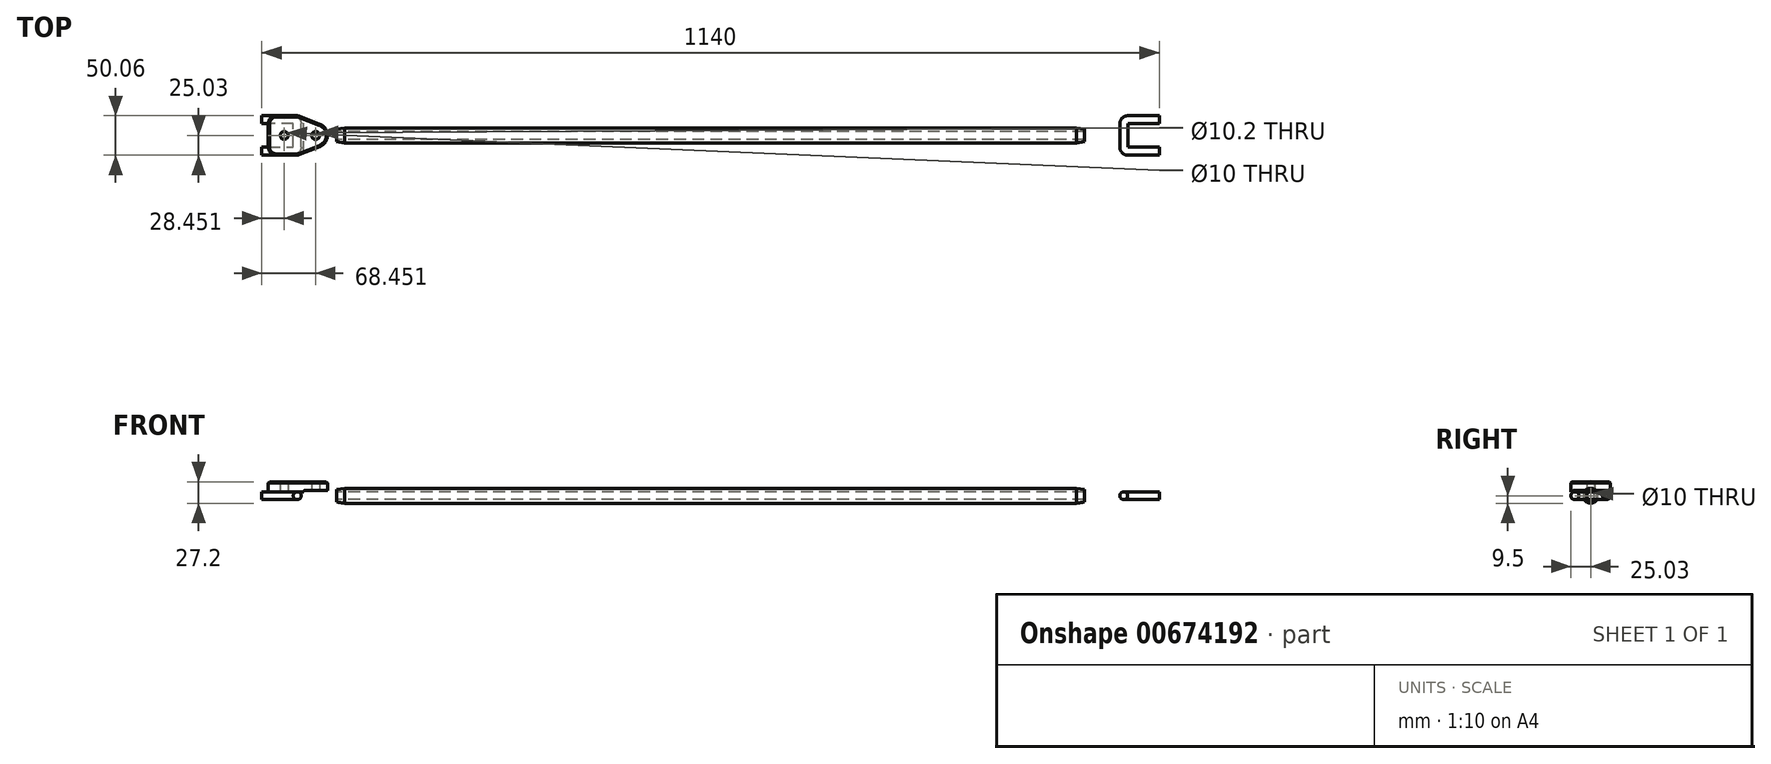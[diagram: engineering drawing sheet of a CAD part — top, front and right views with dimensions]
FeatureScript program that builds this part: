
annotation { "Feature Type Name" : "Feature", "Feature Type Description" : "" }
export const myFeature = defineFeature(function(context is Context, id is Id, definition is map)
    precondition{}
    {
        {
            var Q0;
            Q0=qCreatedBy(makeId("Top.planeOp"),FACE);
            var sketch = newSketch(context, id + "F0", { "sketchPlane" : qUnion([Q0])});
            skLineSegment(sketch, "E0", {"start": v(-525, 0) * mm, "end": v(525, 0) * mm, "construction": true});
            skLineSegment(sketch, "E1", {"start": v(525, 15) * mm, "end": v(525, -15) * mm});
            skLineSegment(sketch, "E2", {"start": v(530, -20) * mm, "end": v(570, -20) * mm});
            skLineSegment(sketch, "E3", {"start": v(530, 20) * mm, "end": v(570, 20) * mm});
            skPoint(sketch, "E4.visualSharp", {"position": v(525, 20) * mm});
            skArc(sketch, "E4.filletArc", {"start": v(530, 20) * mm, "mid": v(526.46, 18.54) * mm, "end": v(525, 15) * mm});
            skPoint(sketch, "E5.visualSharp", {"position": v(525, -20) * mm});
            skArc(sketch, "E5.filletArc", {"start": v(525, -15) * mm, "mid": v(526.46, -18.54) * mm, "end": v(530, -20) * mm});
            skArc(sketch, "E6.MirrorCS", {"start": v(-525, -15) * mm, "mid": v(-526.46, -18.54) * mm, "end": v(-530, -20) * mm});
            skArc(sketch, "E7.MirrorCS", {"start": v(-530, 20) * mm, "mid": v(-526.46, 18.54) * mm, "end": v(-525, 15) * mm});
            skPoint(sketch, "E8.MirrorP", {"position": v(-525, 20) * mm});
            skPoint(sketch, "E9.MirrorP", {"position": v(-525, -20) * mm});
            skLineSegment(sketch, "E10.MirrorCS", {"start": v(-530, -20) * mm, "end": v(-570, -20) * mm});
            skLineSegment(sketch, "E11.MirrorCS", {"start": v(-525, 15) * mm, "end": v(-525, -15) * mm});
            skLineSegment(sketch, "E12.MirrorCS", {"start": v(-530, 20) * mm, "end": v(-570, 20) * mm});
            skSolve(sketch);
        }
        {
            var Q0;
            Q0=qCreatedBy(makeId("Right.planeOp"),FACE);
            cPlane(context, id + "F1", {"entities" : qUnion([Q0]), "cplaneType" : CPlaneType.OFFSET, "offset" : 570 * mm, "width" : 150 * mm, "height" : 150 * mm});
        }
        {
            var Q0;
            Q0=qCreatedBy(makeId("Right.planeOp"),FACE);
            cPlane(context, id + "F2", {"entities" : qUnion([Q0]), "cplaneType" : CPlaneType.OFFSET, "offset" : 570 * mm, "oppositeDirection" : true, "width" : 150 * mm, "height" : 150 * mm});
        }
        {
            var Q0;
            Q0=qCreatedBy(id+"F2.planeOp",FACE);
            var sketch = newSketch(context, id + "F3", { "sketchPlane" : qUnion([Q0])});
            skCircle(sketch, "E13", {"center": v(-20.03, 0) * mm, "radius": 5 * mm});
            skLineSegment(sketch, "E14", {"start": v(0, 9.48) * mm, "end": v(0, -9.24) * mm, "construction": true});
            skSolve(sketch);
        }
        {
            var Q0;
            Q0=makeQuery(id+"F3.imprint","IMPRINT",FACE,{"disambiguationData":[TD([[makeQuery(id+"F3.imprint","IMPRINT",EDGE,{"derivedFrom":sQuery(id+"F3.wireOp",EDGE,"E13")}),1.0]])]});
            var Q1;
            Q1=sQuery(id+"F0.wireOp",EDGE,"E10.MirrorCS");
            var Q2;
            Q2=sQuery(id+"F0.wireOp",EDGE,"E6.MirrorCS");
            var Q3;
            Q3=sQuery(id+"F0.wireOp",EDGE,"E11.MirrorCS");
            var Q4;
            Q4=sQuery(id+"F0.wireOp",EDGE,"E7.MirrorCS");
            var Q5;
            Q5=sQuery(id+"F0.wireOp",EDGE,"E12.MirrorCS");
            sweep(context, id + "F4", {"profiles" : qUnion([Q0]), "path" : qUnion([Q1, Q2, Q3, Q4, Q5])});
        }
        {
            var Q0;
            Q0=qCreatedBy(id+"F1.planeOp",FACE);
            var sketch = newSketch(context, id + "F5", { "sketchPlane" : qUnion([Q0])});
            skCircle(sketch, "E15", {"center": v(20, 0) * mm, "radius": 5 * mm});
            skLineSegment(sketch, "E16", {"start": v(0, 9.53) * mm, "end": v(0, -12.38) * mm, "construction": true});
            skSolve(sketch);
        }
        {
            var Q0;
            Q0=makeQuery(id+"F5.imprint","IMPRINT",FACE,{"disambiguationData":[TD([[makeQuery(id+"F5.imprint","IMPRINT",EDGE,{"derivedFrom":sQuery(id+"F5.wireOp",EDGE,"E15")}),1.0]])]});
            var Q1;
            Q1=sQuery(id+"F0.wireOp",EDGE,"E3");
            var Q2;
            Q2=sQuery(id+"F0.wireOp",EDGE,"E4.filletArc");
            var Q3;
            Q3=sQuery(id+"F0.wireOp",EDGE,"E1");
            var Q4;
            Q4=sQuery(id+"F0.wireOp",EDGE,"E5.filletArc");
            var Q5;
            Q5=sQuery(id+"F0.wireOp",EDGE,"E2");
            sweep(context, id + "F6", {"profiles" : qUnion([Q0]), "path" : qUnion([Q1, Q2, Q3, Q4, Q5])});
        }
        {
            var Q0;
            Q0=qCreatedBy(makeId("Right.planeOp"),FACE);
            var sketch = newSketch(context, id + "F7", { "sketchPlane" : qUnion([Q0])});
            skCircle(sketch, "E17", {"center": v(0, 0) * mm, "radius": 9.5 * mm});
            skCircle(sketch, "E18", {"center": v(0, 0) * mm, "radius": 5 * mm});
            skSolve(sketch);
        }
        {
            var Q0;
            Q0=makeQuery(id+"F7.imprint","IMPRINT",FACE,{"disambiguationData":[TD([[makeQuery(id+"F7.imprint","IMPRINT",EDGE,{"derivedFrom":sQuery(id+"F7.wireOp",EDGE,"E17")}),1.0]])]});
            extrude(context, id + "F8", {"entities" : qUnion([Q0]), "endBound" : BoundingType.SYMMETRIC, "depth" : 950 * mm, "offsetDistance" : 25 * mm});
        }
        {
            var Q0;
            Q0=qCreatedBy(makeId("Top.planeOp"),FACE);
            cPlane(context, id + "F9", {"entities" : qUnion([Q0]), "cplaneType" : CPlaneType.OFFSET, "offset" : 5 * mm, "width" : 150 * mm, "height" : 150 * mm});
        }
        {
            var Q0;
            Q0=qCreatedBy(id+"F9.planeOp",FACE);
            var sketch = newSketch(context, id + "F10", { "sketchPlane" : qUnion([Q0])});
            skLineSegment(sketch, "E19.bottom", {"start": v(-525.95, 25) * mm, "end": v(-551.55, 25) * mm});
            skLineSegment(sketch, "E19.top", {"start": v(-525.95, -25) * mm, "end": v(-551.55, -25) * mm});
            skLineSegment(sketch, "E19.right", {"start": v(-561.55, 15) * mm, "end": v(-561.55, -15) * mm});
            skPoint(sketch, "E19.middle", {"position": v(-524.05, 0) * mm});
            skLineSegment(sketch, "E20", {"start": v(-524.05, 0) * mm, "end": v(-486.55, 0) * mm, "construction": true});
            skArc(sketch, "E21", {"start": v(-496.04, -13.95) * mm, "mid": v(-486.55, 0) * mm, "end": v(-496.04, 13.95) * mm});
            skLineSegment(sketch, "E22", {"start": v(-496.04, 13.95) * mm, "end": v(-522.28, 24.3) * mm});
            skLineSegment(sketch, "E23", {"start": v(-496.04, -13.95) * mm, "end": v(-522.28, -24.3) * mm});
            skCircle(sketch, "E24", {"center": v(-501.55, 0) * mm, "radius": 5.1 * mm});
            skPoint(sketch, "E25.orphan", {"position": v(-486.55, -25) * mm});
            skPoint(sketch, "E19.left.start.orphan", {"position": v(-486.55, 25) * mm});
            skPoint(sketch, "E26.visualSharp", {"position": v(-524.05, 25) * mm});
            skArc(sketch, "E26.filletArc", {"start": v(-522.28, 24.3) * mm, "mid": v(-524.08, 24.82) * mm, "end": v(-525.95, 25) * mm});
            skPoint(sketch, "E27.visualSharp", {"position": v(-561.55, 25) * mm});
            skArc(sketch, "E27.filletArc", {"start": v(-551.55, 25) * mm, "mid": v(-558.62, 22.07) * mm, "end": v(-561.55, 15) * mm});
            skPoint(sketch, "E28.visualSharp", {"position": v(-561.55, -25) * mm});
            skArc(sketch, "E28.filletArc", {"start": v(-561.55, -15) * mm, "mid": v(-558.62, -22.07) * mm, "end": v(-551.55, -25) * mm});
            skLineSegment(sketch, "E29", {"start": v(-524.05, 0) * mm, "end": v(-561.55, 0) * mm, "construction": true});
            skCircle(sketch, "E30", {"center": v(-541.55, 0) * mm, "radius": 5 * mm});
            skLineSegment(sketch, "E31", {"start": v(-525.95, 25) * mm, "end": v(-525.95, -25) * mm, "construction": true});
            skPoint(sketch, "E32.visualSharp", {"position": v(-524.05, -25) * mm});
            skArc(sketch, "E32.filletArc", {"start": v(-525.95, -25) * mm, "mid": v(-524.08, -24.82) * mm, "end": v(-522.28, -24.3) * mm});
            skSolve(sketch);
        }
        {
            var Q0;
            Q0=makeQuery(id+"F10.imprint","IMPRINT",FACE,{"disambiguationData":[TD([[makeQuery(id+"F10.imprint","IMPRINT",EDGE,{"derivedFrom":sQuery(id+"F10.wireOp",EDGE,"E19.bottom")}),1.0]])]});
            extrude(context, id + "F11", {"entities" : qUnion([Q0]), "operationType" : NewBodyOperationType.ADD, "depth" : 12.7 * mm, "offsetDistance" : 25 * mm});
        }
        {
            var Q0;
            Q0=makeQuery(id+"F11.opExtrude","CAP_FACE",FACE,{"disambiguationData":[OSD([sQuery(id+"F10.wireOp",EDGE,"E19.bottom"),sQuery(id+"F10.wireOp",EDGE,"E19.top"),sQuery(id+"F10.wireOp",EDGE,"E19.right"),sQuery(id+"F10.wireOp",EDGE,"E21"),sQuery(id+"F10.wireOp",EDGE,"E22"),sQuery(id+"F10.wireOp",EDGE,"E23"),sQuery(id+"F10.wireOp",EDGE,"E24"),sQuery(id+"F10.wireOp",EDGE,"E26.filletArc"),sQuery(id+"F10.wireOp",EDGE,"E27.filletArc"),sQuery(id+"F10.wireOp",EDGE,"E28.filletArc"),sQuery(id+"F10.wireOp",EDGE,"E30"),sQuery(id+"F10.wireOp",EDGE,"E32.filletArc")])],"isStart":true});
            var sketch = newSketch(context, id + "F12", { "sketchPlane" : qUnion([Q0])});
            skArc(sketch, "E33.0", {"start": v(-496.04, 13.95) * mm, "mid": v(-486.55, 0) * mm, "end": v(-496.04, -13.95) * mm});
            skLineSegment(sketch, "E34.0", {"start": v(-496.04, 13.95) * mm, "end": v(-516.8, 22.14) * mm});
            skLineSegment(sketch, "E35.0", {"start": v(-496.04, -13.95) * mm, "end": v(-516.8, -22.14) * mm});
            skLineSegment(sketch, "E36", {"start": v(-516.8, 22.14) * mm, "end": v(-516.8, -22.14) * mm});
            skPoint(sketch, "E37.orphan", {"position": v(-522.28, 24.3) * mm});
            skPoint(sketch, "E38.orphan", {"position": v(-522.28, -24.3) * mm});
            skSolve(sketch);
        }
        {
            var Q0;
            Q0=makeQuery(id+"F12.imprint","IMPRINT",FACE,{"disambiguationData":[TD([[makeQuery(id+"F12.imprint","IMPRINT",EDGE,{"derivedFrom":sQuery(id+"F12.wireOp",EDGE,"E33.0")}),-1.0]])]});
            extrude(context, id + "F13", {"entities" : qUnion([Q0]), "operationType" : NewBodyOperationType.REMOVE, "oppositeDirection" : true, "depth" : 2 * mm, "offsetDistance" : 25 * mm});
        }
        {
            var Q0;
            Q0=makeQuery(id+"F13.boolean.opBoolean","COPY",EDGE,{"derivedFrom":makeQuery(id+"F13.opExtrude","CAP_EDGE",EDGE,{"disambiguationData":[OSD([sQuery(id+"F12.wireOp",EDGE,"E36")])],"isStart":false})});
            fillet(context, id + "F14", {"entities" : qUnion([Q0]), "radius" : 2 * mm, "tangentPropagation" : true, "allowEdgeOverflow" : false});
        }
        {
            var Q0;
            Q0=makeQuery(id+"F8.opExtrude","CAP_EDGE",EDGE,{"disambiguationData":[OSD([sQuery(id+"F7.wireOp",EDGE,"E17")])],"isStart":true});
            chamfer(context, id + "F15", {"entities" : qUnion([Q0]), "chamferType" : ChamferType.TWO_OFFSETS, "width1" : 10 * mm, "oppositeDirection" : false, "width2" : 1.5 * mm, "tangentPropagation" : true});
        }
        {
            var Q0;
            Q0=makeQuery(id+"F8.opExtrude","CAP_EDGE",EDGE,{"disambiguationData":[OSD([sQuery(id+"F7.wireOp",EDGE,"E17")])],"isStart":false});
            chamfer(context, id + "F16", {"entities" : qUnion([Q0]), "chamferType" : ChamferType.TWO_OFFSETS, "width1" : 1.5 * mm, "oppositeDirection" : false, "width2" : 10 * mm, "tangentPropagation" : true});
        }
        {
            var Q0;
            Q0=makeQuery(id+"F11.opExtrude","CAP_EDGE",EDGE,{"disambiguationData":[OSD([sQuery(id+"F10.wireOp",EDGE,"E23")])],"isStart":false});
            chamfer(context, id + "F17", {"entities" : qUnion([Q0]), "width" : 1.5 * mm, "tangentPropagation" : true});
        }
    });
